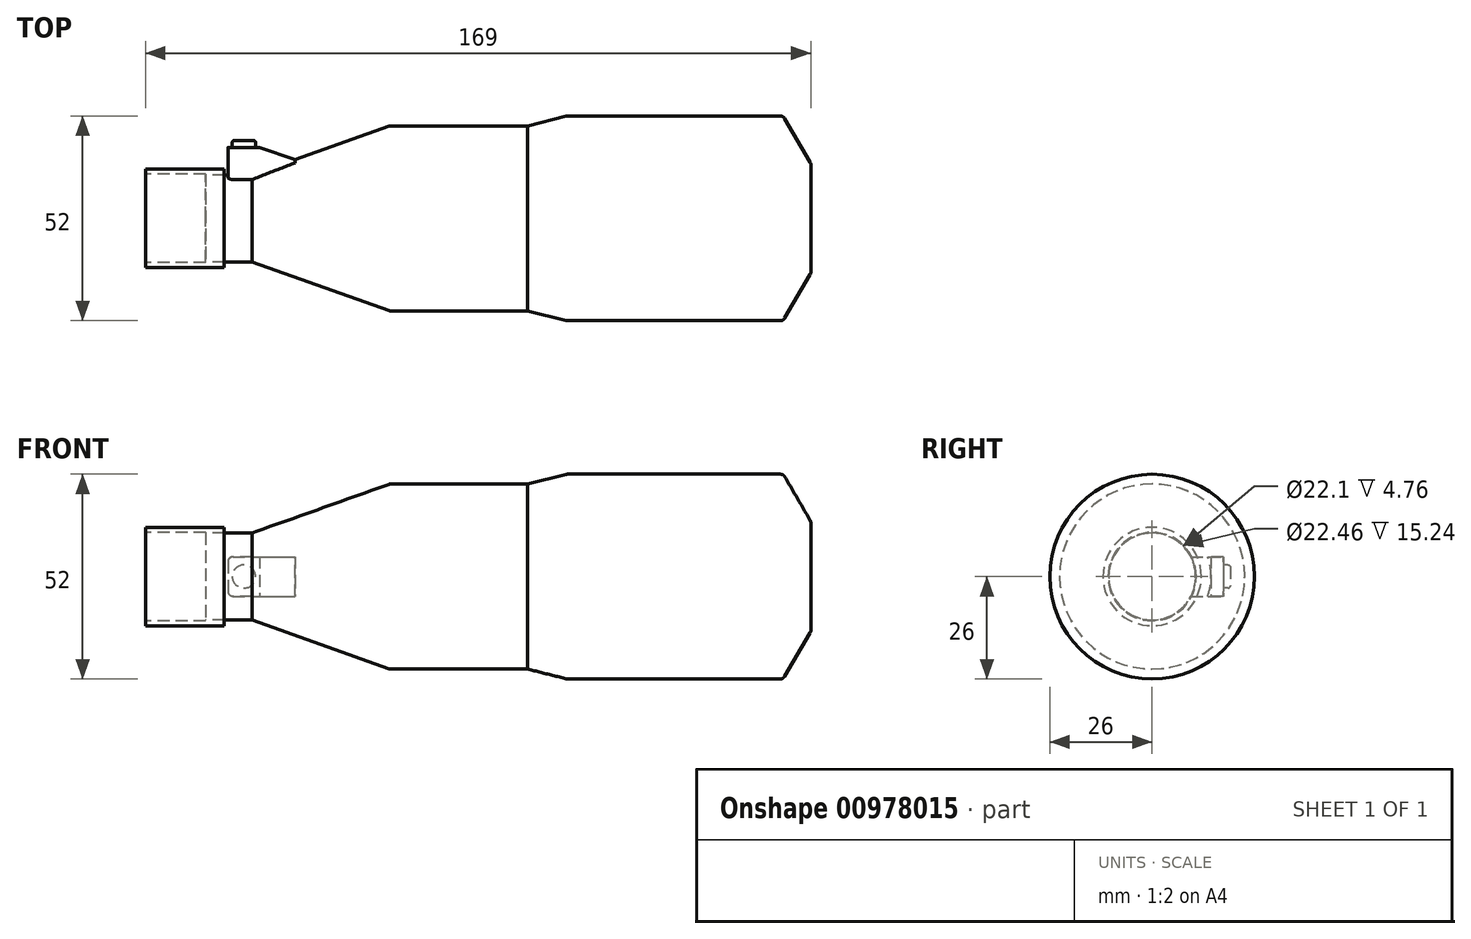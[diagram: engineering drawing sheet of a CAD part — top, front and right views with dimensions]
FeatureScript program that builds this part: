
annotation { "Feature Type Name" : "Feature", "Feature Type Description" : "" }
export const myFeature = defineFeature(function(context is Context, id is Id, definition is map)
    precondition{}
    {
        {
            var Q0;
            Q0=qCreatedBy(makeId("Top.planeOp"),FACE);
            var sketch = newSketch(context, id + "F0", { "sketchPlane" : qUnion([Q0])});
            skLineSegment(sketch, "E0", {"start": v(-55.12, 0) * mm, "end": v(123.88, 0) * mm});
            skLineSegment(sketch, "E1.bottom", {"start": v(-55.12, 0) * mm, "end": v(-35.12, 0) * mm});
            skLineSegment(sketch, "E1.top", {"start": v(-55.12, 12.5) * mm, "end": v(-35.12, 12.5) * mm});
            skLineSegment(sketch, "E1.left", {"start": v(-55.12, 0) * mm, "end": v(-55.12, 12.5) * mm});
            skLineSegment(sketch, "E1.right", {"start": v(-35.12, 0) * mm, "end": v(-35.12, 12.5) * mm});
            skLineSegment(sketch, "E2.bottom", {"start": v(-55.12, 0) * mm, "end": v(-28.12, 0) * mm});
            skLineSegment(sketch, "E2.top", {"start": v(-55.12, 11.05) * mm, "end": v(-28.12, 11.05) * mm});
            skLineSegment(sketch, "E2.left", {"start": v(-55.12, 0) * mm, "end": v(-55.12, 11.05) * mm});
            skLineSegment(sketch, "E2.right", {"start": v(-28.12, 0) * mm, "end": v(-28.12, 11.05) * mm});
            skLineSegment(sketch, "E3", {"start": v(-55.12, 0) * mm, "end": v(6.88, 0) * mm});
            skLineSegment(sketch, "E4", {"start": v(6.88, 0) * mm, "end": v(6.88, 23.5) * mm});
            skLineSegment(sketch, "E5", {"start": v(-28.12, 11.05) * mm, "end": v(6.88, 23.5) * mm});
            skLineSegment(sketch, "E6", {"start": v(6.88, 23.5) * mm, "end": v(41.88, 23.5) * mm});
            skLineSegment(sketch, "E7", {"start": v(41.88, 23.5) * mm, "end": v(41.88, 0) * mm});
            skLineSegment(sketch, "E8", {"start": v(41.88, 0) * mm, "end": v(51.88, 0) * mm});
            skLineSegment(sketch, "E9", {"start": v(51.88, 0) * mm, "end": v(51.88, 26) * mm});
            skLineSegment(sketch, "E10", {"start": v(51.88, 26) * mm, "end": v(41.88, 23.5) * mm});
            skLineSegment(sketch, "E11", {"start": v(51.88, 26) * mm, "end": v(106.88, 26) * mm});
            skLineSegment(sketch, "E12", {"start": v(106.88, 0) * mm, "end": v(113.88, 0) * mm});
            skLineSegment(sketch, "E13", {"start": v(113.88, 0) * mm, "end": v(113.88, 14) * mm});
            skLineSegment(sketch, "E14", {"start": v(113.88, 14) * mm, "end": v(106.88, 26) * mm});
            skLineSegment(sketch, "E15.bottom", {"start": v(123.88, 0) * mm, "end": v(113.88, 0) * mm});
            skLineSegment(sketch, "E15.top", {"start": v(123.88, 14) * mm, "end": v(113.88, 14) * mm});
            skLineSegment(sketch, "E15.left", {"start": v(123.88, 0) * mm, "end": v(123.88, 14) * mm});
            skLineSegment(sketch, "E16", {"start": v(-34.2, 11.05) * mm, "end": v(-34.2, 18.05) * mm});
            skLineSegment(sketch, "E17", {"start": v(-34.2, 18.05) * mm, "end": v(-26.2, 18.05) * mm});
            skLineSegment(sketch, "E18", {"start": v(-35.12, 0) * mm, "end": v(-17.12, 0) * mm});
            skLineSegment(sketch, "E19", {"start": v(-26.2, 18.05) * mm, "end": v(-17.12, 14.96) * mm});
            skSolve(sketch);
        }
        {
            var Q0;
            {var subQ5=sQuery(id+"F0.wireOp",EDGE,"E2.left");Q0=makeQuery(id+"F0.imprint","IMPRINT",FACE,{"disambiguationData":[TD([[makeQuery(id+"F0.imprint","IMPRINT",EDGE,{"derivedFrom":subQ5}),-1.0]])]});}
            var Q1;
            {var subQ0=sQuery(id+"F0.wireOp",EDGE,"E1.top");Q1=makeQuery(id+"F0.imprint","IMPRINT",FACE,{"disambiguationData":[TD([[makeQuery(id+"F0.imprint","IMPRINT",EDGE,{"derivedFrom":subQ0}),-1.0]])]});}
            var Q2;
            {var subQ0=sQuery(id+"F0.wireOp",EDGE,"E2.right");Q2=makeQuery(id+"F0.imprint","IMPRINT",FACE,{"disambiguationData":[TD([[makeQuery(id+"F0.imprint","IMPRINT",EDGE,{"derivedFrom":subQ0}),1.0]])]});}
            var Q3;
            {var subQ1=sQuery(id+"F0.wireOp",EDGE,"E2.right");Q3=makeQuery(id+"F0.imprint","IMPRINT",FACE,{"disambiguationData":[TD([[makeQuery(id+"F0.imprint","IMPRINT",EDGE,{"derivedFrom":subQ1}),-1.0]])]});}
            var Q4;
            {var subQ0=sQuery(id+"F0.wireOp",EDGE,"E4");Q4=makeQuery(id+"F0.imprint","IMPRINT",FACE,{"disambiguationData":[TD([[makeQuery(id+"F0.imprint","IMPRINT",EDGE,{"derivedFrom":subQ0}),-1.0]])]});}
            var Q5;
            Q5=makeQuery(id+"F0.imprint","IMPRINT",FACE,{"disambiguationData":[TD([[makeQuery(id+"F0.imprint","IMPRINT",EDGE,{"derivedFrom":sQuery(id+"F0.wireOp",EDGE,"E7")}),1.0]])]});
            var Q6;
            {var subQ1=sQuery(id+"F0.wireOp",EDGE,"E9");Q6=makeQuery(id+"F0.imprint","IMPRINT",FACE,{"disambiguationData":[TD([[makeQuery(id+"F0.imprint","IMPRINT",EDGE,{"derivedFrom":subQ1}),-1.0]])]});}
            var Q7;
            Q7=makeQuery(id+"F0.imprint","IMPRINT",FACE,{"disambiguationData":[TD([[makeQuery(id+"F0.imprint","IMPRINT",EDGE,{"derivedFrom":sQuery(id+"F0.wireOp",EDGE,"E15.bottom")}),-1.0]])]});
            var Q8;
            Q8=sQuery(id+"F0.wireOp",EDGE,"E0");
            revolve(context, id + "F1", {"surfaceOperationType" : NewSurfaceOperationType.NEW, "entities" : qUnion([Q0, Q1, Q2, Q3, Q4, Q5, Q6, Q7]), "axis" : qUnion([Q8]), "revolveType" : RevolveType.FULL});
        }
        {
            var Q0;
            {var subQ4=sQuery(id+"F0.wireOp",EDGE,"E16");Q0=makeQuery(id+"F0.imprint","IMPRINT",FACE,{"disambiguationData":[TD([[makeQuery(id+"F0.imprint","IMPRINT",EDGE,{"derivedFrom":subQ4}),-1.0]])]});}
            extrude(context, id + "F2", {"entities" : qUnion([Q0]), "depth" : 5 * mm, "offsetDistance" : 25.4 * mm});
        }
        {
            var Q0;
            {var subQ4=sQuery(id+"F0.wireOp",EDGE,"E16");Q0=makeQuery(id+"F0.imprint","IMPRINT",FACE,{"disambiguationData":[TD([[makeQuery(id+"F0.imprint","IMPRINT",EDGE,{"derivedFrom":subQ4}),-1.0]])]});}
            extrude(context, id + "F3", {"entities" : qUnion([Q0]), "operationType" : NewBodyOperationType.ADD, "oppositeDirection" : true, "depth" : 5 * mm, "offsetDistance" : 25.4 * mm});
        }
        {
            var Q0;
            {var subQ0=sQuery(id+"F0.wireOp",EDGE,"E2.top");Q0=makeQuery(id+"F3.boolean.opBoolean","MERGE",FACE,{"derivedFrom":[makeQuery(id+"F2.opExtrude","SWEPT_FACE",FACE,{"disambiguationData":[OSD([subQ0])]}),makeQuery(id+"F3.opExtrude","SWEPT_FACE",FACE,{"disambiguationData":[OSD([subQ0])]})]});}
            var Q1;
            {var subQ0=sQuery(id+"F0.wireOp",EDGE,"E5");Q1=makeQuery(id+"F3.boolean.opBoolean","MERGE",FACE,{"derivedFrom":[makeQuery(id+"F2.opExtrude","SWEPT_FACE",FACE,{"disambiguationData":[OSD([subQ0])]}),makeQuery(id+"F3.opExtrude","SWEPT_FACE",FACE,{"disambiguationData":[OSD([subQ0])]})]});}
            extrude(context, id + "F4", {"entities" : qUnion([Q0, Q1]), "operationType" : NewBodyOperationType.ADD, "depth" : 10 * mm, "offsetDistance" : 25.4 * mm});
        }
        {
            var Q0;
            {var subQ0=sQuery(id+"F0.wireOp",EDGE,"E17");Q0=makeQuery(id+"F3.boolean.opBoolean","MERGE",FACE,{"derivedFrom":[makeQuery(id+"F2.opExtrude","SWEPT_FACE",FACE,{"disambiguationData":[OSD([subQ0])]}),makeQuery(id+"F3.opExtrude","SWEPT_FACE",FACE,{"disambiguationData":[OSD([subQ0])]})]});}
            var sketch = newSketch(context, id + "F5", { "sketchPlane" : qUnion([Q0])});
            skCircle(sketch, "E20", {"center": v(30.15, 0) * mm, "radius": 2.94 * mm});
            skSolve(sketch);
        }
        {
            var Q0;
            Q0=makeQuery(id+"F2.opExtrude","CAP_EDGE",EDGE,{"disambiguationData":[OSD([sQuery(id+"F0.wireOp",EDGE,"E16")])],"isStart":false});
            var Q1;
            Q1=makeQuery(id+"F3.opExtrude","CAP_EDGE",EDGE,{"disambiguationData":[OSD([sQuery(id+"F0.wireOp",EDGE,"E16")])],"isStart":false});
            var Q2;
            {var subQ0=sQuery(id+"F0.wireOp",EDGE,"E16");var subQ1=sQuery(id+"F0.wireOp",EDGE,"E2.top");Q2=makeQuery(id+"F4.opExtrude","SWEPT_EDGE",EDGE,{"disambiguationData":[OSD([subQ1,subQ0]),TDD([makeQuery(id+"F2.opExtrude","CAP_VERTEX",VERTEX,{"disambiguationData":[OSD([subQ1,subQ0])],"isStart":false})])]});}
            var Q3;
            {var subQ0=sQuery(id+"F0.wireOp",EDGE,"E16");var subQ1=sQuery(id+"F0.wireOp",EDGE,"E2.top");Q3=makeQuery(id+"F4.opExtrude","SWEPT_EDGE",EDGE,{"disambiguationData":[OSD([subQ1,subQ0]),TDD([makeQuery(id+"F3.opExtrude","CAP_VERTEX",VERTEX,{"disambiguationData":[OSD([subQ1,subQ0])],"isStart":false})])]});}
            var Q4;
            Q4=makeQuery(id+"F1.opRevolve","SWEPT_EDGE",EDGE,{"disambiguationData":[OSD([sQuery(id+"F0.wireOp",EDGE,"E15.top"),sQuery(id+"F0.wireOp",EDGE,"E15.left")])]});
            var Q5;
            Q5=makeQuery(id+"F1.opRevolve","SWEPT_EDGE",EDGE,{"disambiguationData":[OSD([sQuery(id+"F0.wireOp",EDGE,"E11"),sQuery(id+"F0.wireOp",EDGE,"E14")])]});
            var Q6;
            Q6=makeQuery(id+"F1.opRevolve","SWEPT_EDGE",EDGE,{"disambiguationData":[OSD([sQuery(id+"F0.wireOp",EDGE,"E9"),sQuery(id+"F0.wireOp",EDGE,"E10"),sQuery(id+"F0.wireOp",EDGE,"E11")])]});
            var Q7;
            Q7=makeQuery(id+"F1.opRevolve","SWEPT_EDGE",EDGE,{"disambiguationData":[OSD([sQuery(id+"F0.wireOp",EDGE,"E4"),sQuery(id+"F0.wireOp",EDGE,"E5"),sQuery(id+"F0.wireOp",EDGE,"E6")])]});
            fillet(context, id + "F6", {"entities" : qUnion([Q0, Q1, Q2, Q3, Q4, Q5, Q6, Q7]), "radius" : 1.27 * mm, "tangentPropagation" : true, "allowEdgeOverflow" : false});
        }
        {
            var Q0;
            Q0=makeQuery(id+"F1.opRevolve","SWEPT_FACE",FACE,{"disambiguationData":[OSD([sQuery(id+"F0.wireOp",EDGE,"E1.left"),sQuery(id+"F0.wireOp",EDGE,"E2.left")])]});
            var sketch = newSketch(context, id + "F7", { "sketchPlane" : qUnion([Q0])});
            skCircle(sketch, "E21.0", {"center": v(0, 0) * mm, "radius": 11.23 * mm});
            skSolve(sketch);
        }
        {
            var Q0;
            Q0=makeQuery(id+"F7.imprint","IMPRINT",FACE,{"disambiguationData":[TD([[makeQuery(id+"F7.imprint","IMPRINT",EDGE,{"derivedFrom":sQuery(id+"F7.wireOp",EDGE,"E21.0")}),1.0]])]});
            extrude(context, id + "F8", {"entities" : qUnion([Q0]), "operationType" : NewBodyOperationType.REMOVE, "oppositeDirection" : true, "depth" : 15.24 * mm, "offsetDistance" : 25.4 * mm});
        }
        {
            var Q0;
            Q0=makeQuery(id+"F5.imprint","IMPRINT",FACE,{"disambiguationData":[TD([[makeQuery(id+"F5.imprint","IMPRINT",EDGE,{"derivedFrom":sQuery(id+"F5.wireOp",EDGE,"E20")}),1.0]])]});
            extrude(context, id + "F9", {"entities" : qUnion([Q0]), "operationType" : NewBodyOperationType.ADD, "depth" : 1.78 * mm, "offsetDistance" : 25.4 * mm});
        }
        {
            var Q0;
            Q0=makeQuery(id+"F9.opExtrude","CAP_EDGE",EDGE,{"disambiguationData":[OSD([sQuery(id+"F5.wireOp",EDGE,"E20")])],"isStart":false});
            fillet(context, id + "F10", {"entities" : qUnion([Q0]), "radius" : 0.55 * mm, "tangentPropagation" : true, "allowEdgeOverflow" : false});
        }
    });
